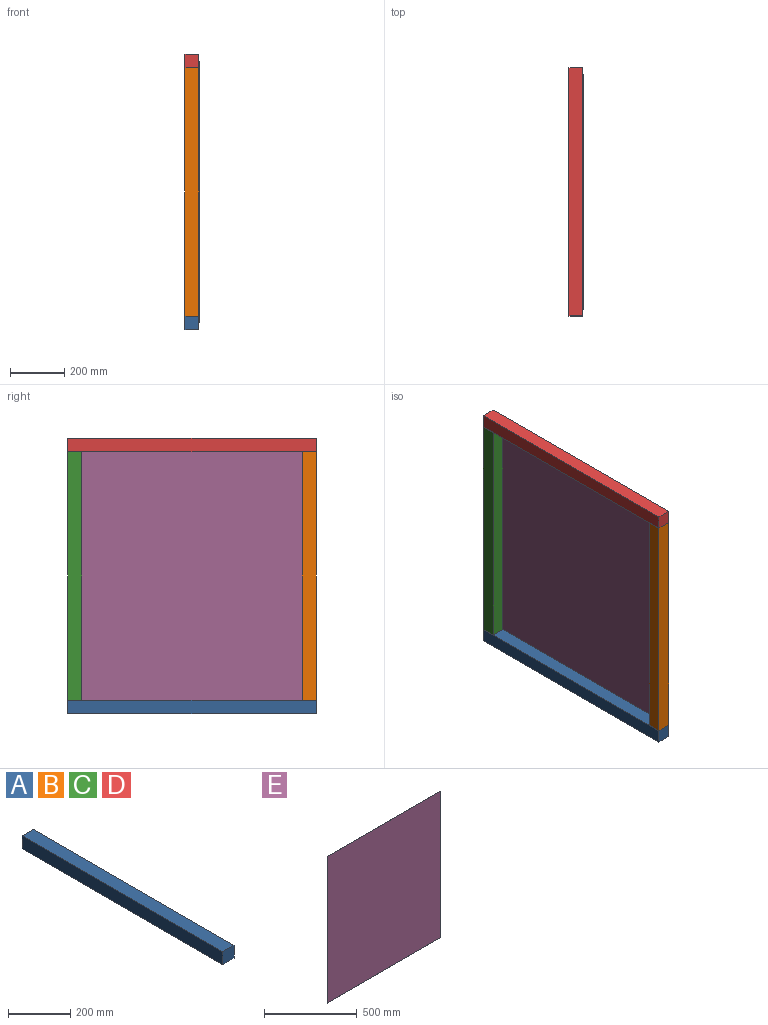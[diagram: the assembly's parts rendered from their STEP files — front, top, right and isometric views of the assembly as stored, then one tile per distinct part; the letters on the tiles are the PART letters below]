
ASSEMBLY  parts=5 mates=4
PART A: 6 faces, bbox 50.8x914.4x50.8 mm
  f0: plane 914.4x50.8mm, normal (1,0,0), area 46451.5mm2, adj f1,f3,f4,f5
  f1: plane 914.4x50.8mm, normal (0,0,1), area 46451.5mm2, adj f0,f2,f4,f5
  f2: plane 914.4x50.8mm, normal (-1,0,0), area 46451.5mm2, adj f1,f3,f4,f5
  f3: plane 914.4x50.8mm, normal (0,0,-1), area 46451.5mm2, adj f0,f2,f4,f5
  f4: plane 50.8x50.8mm, normal (0,-1,0), area 2580.6mm2, adj f0,f1,f2,f3
  f5: plane 50.8x50.8mm, normal (0,1,0), area 2580.6mm2, adj f0,f1,f2,f3
PART B: same geometry as A
PART C: same geometry as A
PART D: same geometry as A
PART E: 6 faces, bbox 863.6x0.8x965.2 mm
  f0: plane 965.2x0.81mm, normal (-1,0,0), area 784.5mm2, adj f1,f3,f4,f5
  f1: plane 863.6x0.81mm, normal (0,0,-1), area 701.9mm2, adj f0,f2,f4,f5
  f2: plane 965.2x0.81mm, normal (1,0,0), area 784.5mm2, adj f1,f3,f4,f5
  f3: plane 863.6x0.81mm, normal (0,0,1), area 701.9mm2, adj f0,f2,f4,f5
  f4: plane 965.2x863.6mm, normal (0,-1,0), area 833546.7mm2, adj f0,f1,f2,f3
  f5: plane 965.2x863.6mm, normal (0,1,0), area 833546.7mm2, adj f0,f1,f2,f3
PLACE A at identity fixed
PLACE B rot(axis=(1,0,0),90deg) t=(0,-889,939.8)mm
PLACE C rot(axis=(-1,0,0),90deg) t=(0,-25.4,25.4)mm
PLACE D rot(axis=(0,1,0),90deg) t=(0,0,965.2)mm
PLACE E rot(axis=(0,0,1),90deg) t=(25.4,-889,0)mm
MATE planar C.f5 <-> A.f1  axis (0,0,1) through (0,0,25.4)mm
MATE fastened B.f4 <-> A.f1  axis (0,0,-1) through (0,-914.4,25.4)mm
MATE fastened A.f0 <-> E.f5  axis (1,0,0) through (25.4,-889,0)mm
MATE fastened D.f0 <-> B.f5  axis (0,0,-1) through (0,-914.4,939.8)mm
